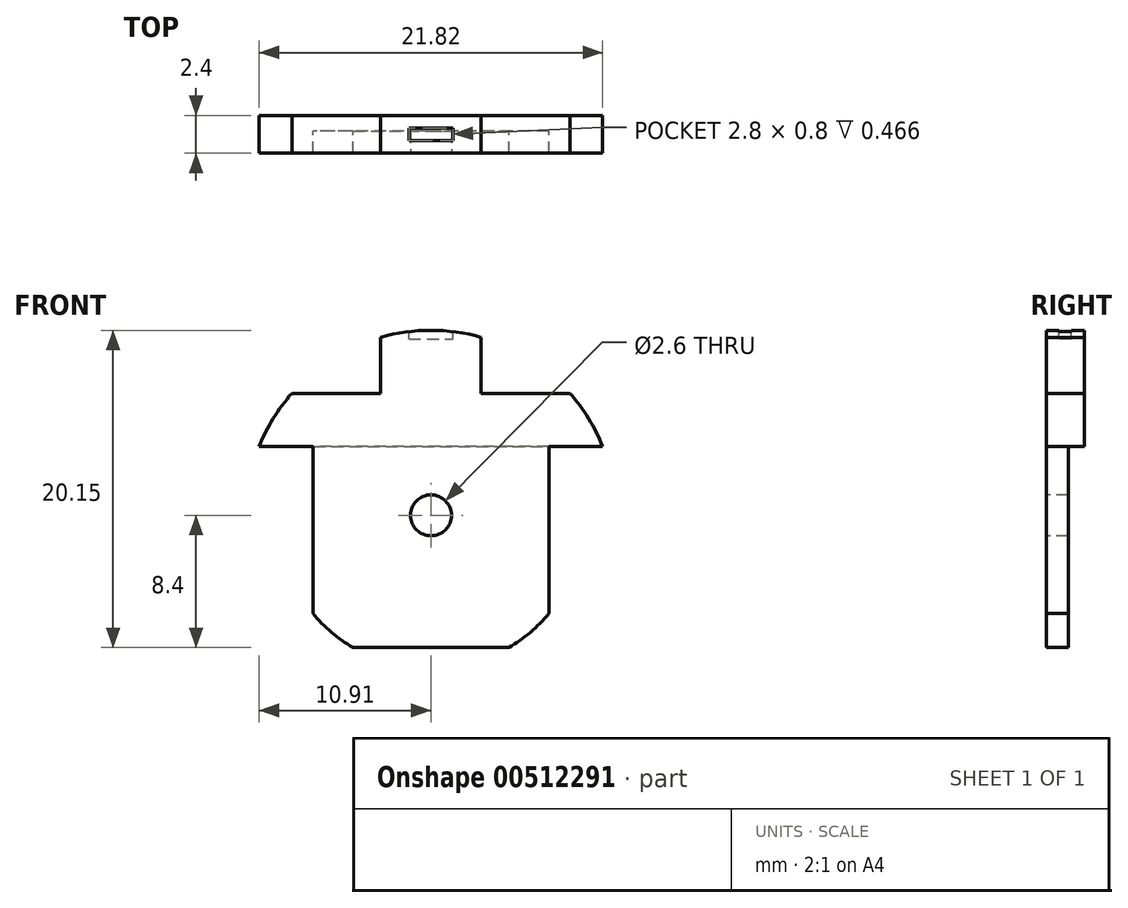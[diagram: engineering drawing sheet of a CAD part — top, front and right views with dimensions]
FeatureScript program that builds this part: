
annotation { "Feature Type Name" : "Feature", "Feature Type Description" : "" }
export const myFeature = defineFeature(function(context is Context, id is Id, definition is map)
    precondition{}
    {
        {
            var Q0;
            Q0=qCreatedBy(makeId("Front.planeOp"),FACE);
            var sketch = newSketch(context, id + "F0", { "sketchPlane" : qUnion([Q0])});
            skArc(sketch, "E0", {"start": v(-7.5, -6.23) * mm, "mid": v(-6.32, -7.43) * mm, "end": v(-4.94, -8.4) * mm});
            skLineSegment(sketch, "E1", {"start": v(-10.9, 4.37) * mm, "end": v(-7.5, 4.37) * mm});
            skArc(sketch, "E2", {"start": v(10.9, 4.37) * mm, "mid": v(0, 11.75) * mm, "end": v(-10.9, 4.37) * mm});
            skLineSegment(sketch, "E3.trimOffspring", {"start": v(7.5, 4.37) * mm, "end": v(10.9, 4.37) * mm});
            skLineSegment(sketch, "E4", {"start": v(0, -9.75) * mm, "end": v(0, 11.75) * mm, "construction": true});
            skLineSegment(sketch, "E5", {"start": v(-7.5, -6.23) * mm, "end": v(-7.5, 4.37) * mm});
            skLineSegment(sketch, "E6", {"start": v(7.5, -6.23) * mm, "end": v(7.5, 4.37) * mm});
            skPoint(sketch, "E7.orphan", {"position": v(7.5, 2.99) * mm});
            skPoint(sketch, "E8.orphan", {"position": v(-7.5, 2.99) * mm});
            skLineSegment(sketch, "E9", {"start": v(4.94, -8.4) * mm, "end": v(-4.94, -8.4) * mm});
            skArc(sketch, "E10.trimOffspring", {"start": v(4.94, -8.4) * mm, "mid": v(6.32, -7.43) * mm, "end": v(7.5, -6.23) * mm});
            skSolve(sketch);
        }
        {
            var Q0;
            Q0=qSketchRegion(id+"F0",true);
            extrude(context, id + "F1", {"entities" : qUnion([Q0]), "depth" : 2.4 * mm, "offsetDistance" : 25 * mm});
        }
        {
            var Q0;
            Q0=qCreatedBy(makeId("Right.planeOp"),FACE);
            var sketch = newSketch(context, id + "F2", { "sketchPlane" : qUnion([Q0])});
            skLineSegment(sketch, "E11.0", {"start": v(-1, 4.37) * mm, "end": v(0, 4.37) * mm});
            skLineSegment(sketch, "E12.0", {"start": v(0, -10.63) * mm, "end": v(0, 4.37) * mm});
            skLineSegment(sketch, "E13", {"start": v(-1, 4.37) * mm, "end": v(-1, -10.63) * mm});
            skLineSegment(sketch, "E14", {"start": v(-1, -10.63) * mm, "end": v(0, -10.63) * mm});
            skPoint(sketch, "E15.orphan", {"position": v(-2.4, 4.37) * mm});
            skPoint(sketch, "E16.orphan", {"position": v(0, -6.23) * mm});
            skSolve(sketch);
        }
        {
            var Q0;
            Q0=qSketchRegion(id+"F2",true);
            extrude(context, id + "F3", {"entities" : qUnion([Q0]), "operationType" : NewBodyOperationType.REMOVE, "endBound" : BoundingType.SYMMETRIC, "depth" : 25 * mm, "offsetDistance" : 25 * mm});
        }
        {
            var Q0;
            Q0=qCreatedBy(makeId("Top.planeOp"),FACE);
            cPlane(context, id + "F4", {"entities" : qUnion([Q0]), "cplaneType" : CPlaneType.OFFSET, "offset" : 12 * mm, "width" : 150 * mm, "height" : 150 * mm});
        }
        {
            var Q0;
            Q0=qCreatedBy(id+"F4.planeOp",FACE);
            var sketch = newSketch(context, id + "F5", { "sketchPlane" : qUnion([Q0])});
            skLineSegment(sketch, "E17", {"start": v(0, 0) * mm, "end": v(0, -5.95) * mm, "construction": true});
            skLineSegment(sketch, "E18", {"start": v(-4.38, -1.2) * mm, "end": v(4.62, -1.2) * mm, "construction": true});
            skLineSegment(sketch, "E19.left", {"start": v(-1.4, -0.8) * mm, "end": v(-1.4, -1.6) * mm});
            skLineSegment(sketch, "E19.right", {"start": v(1.4, -0.8) * mm, "end": v(1.4, -1.6) * mm});
            skLineSegment(sketch, "E20.trimOffspring", {"start": v(-1.4, -0.8) * mm, "end": v(1.4, -0.8) * mm});
            skLineSegment(sketch, "E21.trimOffspring", {"start": v(-1.4, -1.6) * mm, "end": v(1.4, -1.6) * mm});
            skSolve(sketch);
        }
        {
            var Q0;
            Q0=qSketchRegion(id+"F5",true);
            extrude(context, id + "F6", {"entities" : qUnion([Q0]), "operationType" : NewBodyOperationType.REMOVE, "oppositeDirection" : true, "depth" : .8 * mm, "offsetDistance" : 25 * mm});
        }
        {
            var Q0;
            Q0=makeQuery(id+"F1.opExtrude","CAP_FACE",FACE,{"disambiguationData":[OSD([sQuery(id+"F0.wireOp",EDGE,"E0"),sQuery(id+"F0.wireOp",EDGE,"E1"),sQuery(id+"F0.wireOp",EDGE,"E2"),sQuery(id+"F0.wireOp",EDGE,"E3.trimOffspring"),sQuery(id+"F0.wireOp",EDGE,"E5"),sQuery(id+"F0.wireOp",EDGE,"E6"),sQuery(id+"F0.wireOp",EDGE,"E9"),sQuery(id+"F0.wireOp",EDGE,"E10.trimOffspring")])],"isStart":false});
            var sketch = newSketch(context, id + "F7", { "sketchPlane" : qUnion([Q0])});
            skLineSegment(sketch, "E22", {"start": v(-3.2, 11.3) * mm, "end": v(-3.2, 7.75) * mm});
            skLineSegment(sketch, "E23", {"start": v(-3.2, 7.75) * mm, "end": v(-8.83, 7.75) * mm});
            skArc(sketch, "E24.0", {"start": v(8.83, 7.75) * mm, "mid": v(6.27, 9.94) * mm, "end": v(3.2, 11.3) * mm});
            skPoint(sketch, "E25.orphan", {"position": v(-10.9, 4.37) * mm});
            skLineSegment(sketch, "E26", {"start": v(3.2, 11.3) * mm, "end": v(3.2, 7.75) * mm});
            skLineSegment(sketch, "E27", {"start": v(3.2, 7.75) * mm, "end": v(8.83, 7.75) * mm});
            skLineSegment(sketch, "E28", {"start": v(0, 0) * mm, "end": v(0, 11.75) * mm, "construction": true});
            skArc(sketch, "E29.trimOffspring", {"start": v(-3.2, 11.3) * mm, "mid": v(-6.27, 9.94) * mm, "end": v(-8.83, 7.75) * mm});
            skPoint(sketch, "E30.orphan", {"position": v(10.9, 4.37) * mm});
            skSolve(sketch);
        }
        {
            var Q0;
            Q0 = qSketchRegion(id + "F7", true);
            extrude(context, id + "F8", {"entities" : qUnion([Q0]), "operationType" : NewBodyOperationType.REMOVE, "endBound" : BoundingType.THROUGH_ALL, "oppositeDirection" : true, "depth" : 25 * mm, "offsetDistance" : 25 * mm});
        }
        {
            var Q0;
            Q0=makeQuery(id+"F1.opExtrude","CAP_FACE",FACE,{"disambiguationData":[OSD([sQuery(id+"F0.wireOp",EDGE,"E0"),sQuery(id+"F0.wireOp",EDGE,"E1"),sQuery(id+"F0.wireOp",EDGE,"E2"),sQuery(id+"F0.wireOp",EDGE,"E3.trimOffspring"),sQuery(id+"F0.wireOp",EDGE,"E5"),sQuery(id+"F0.wireOp",EDGE,"E6"),sQuery(id+"F0.wireOp",EDGE,"E9"),sQuery(id+"F0.wireOp",EDGE,"E10.trimOffspring")])],"isStart":false});
            var sketch = newSketch(context, id + "F9", { "sketchPlane" : qUnion([Q0])});
            skArc(sketch, "E31.0", {"start": v(4.94, -8.4) * mm, "mid": v(6.32, -7.43) * mm, "end": v(7.5, -6.23) * mm, "construction": true});
            skArc(sketch, "E32.0", {"start": v(10.9, 4.37) * mm, "mid": v(10.01, 6.15) * mm, "end": v(8.83, 7.75) * mm, "construction": true});
            skCircle(sketch, "E33", {"center": v(0, 0) * mm, "radius": 1.3 * mm});
            skSolve(sketch);
        }
        {
            var Q0;
            Q0 = qSketchRegion(id + "F9", true);
            extrude(context, id + "F10", {"entities" : qUnion([Q0]), "operationType" : NewBodyOperationType.REMOVE, "endBound" : BoundingType.THROUGH_ALL, "oppositeDirection" : true, "depth" : 25 * mm, "offsetDistance" : 25 * mm});
        }
    });
